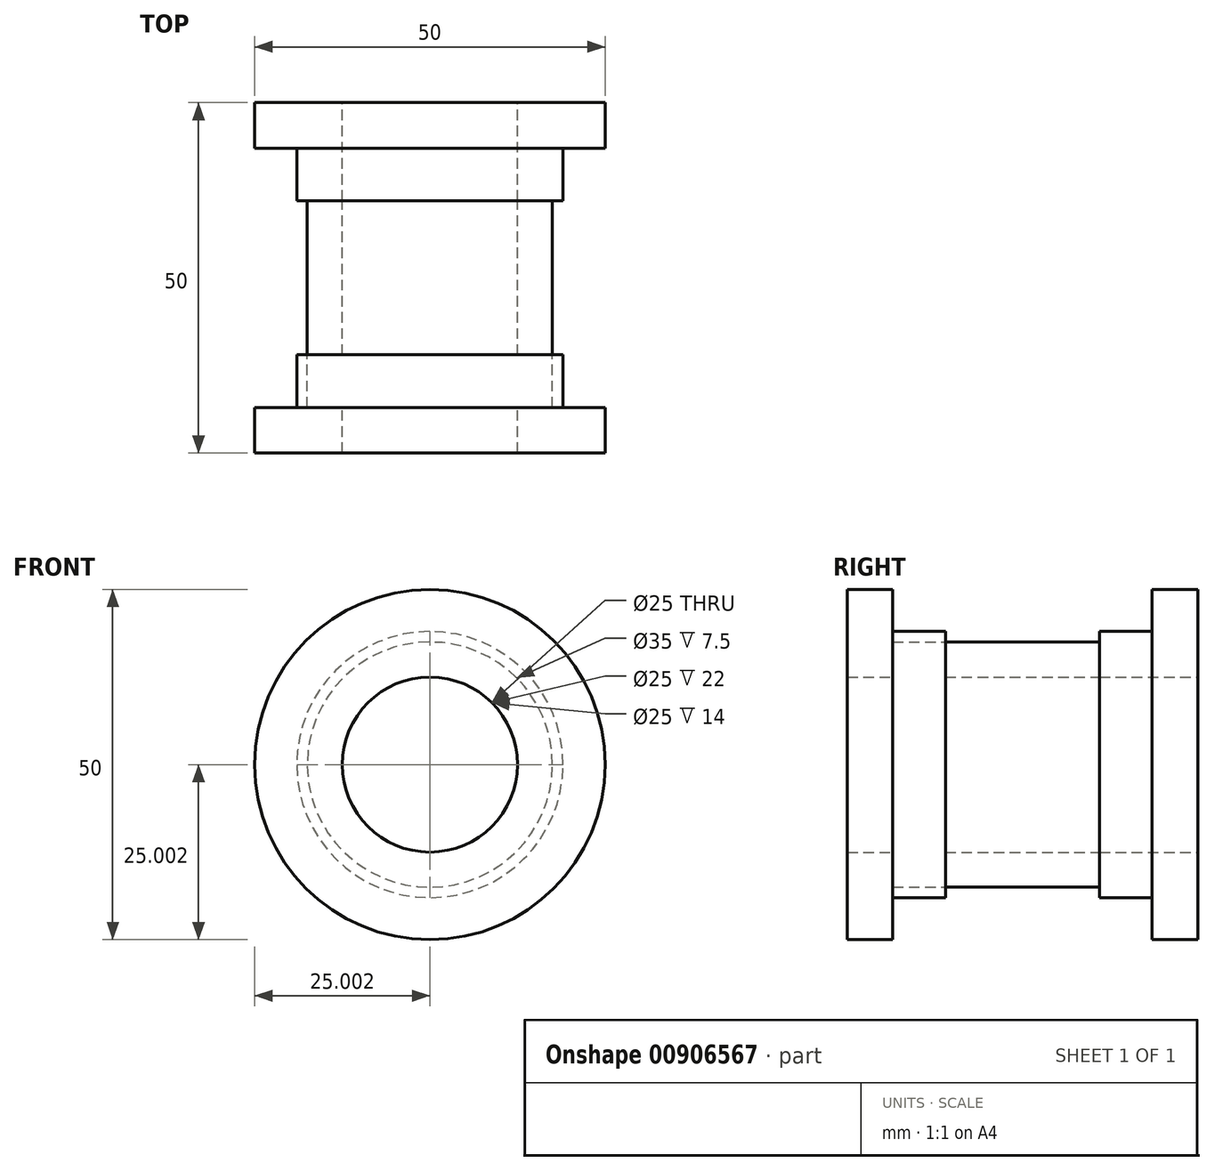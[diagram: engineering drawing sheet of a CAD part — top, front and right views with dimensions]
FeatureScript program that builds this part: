
annotation { "Feature Type Name" : "Feature", "Feature Type Description" : "" }
export const myFeature = defineFeature(function(context is Context, id is Id, definition is map)
    precondition{}
    {
        {
            var Q0;
            Q0=qCreatedBy(makeId("Front.planeOp"),FACE);
            var sketch = newSketch(context, id + "F0", { "sketchPlane" : qUnion([Q0])});
            skCircle(sketch, "E0", {"center": v(-103.9, 30.25) * mm, "radius": 25 * mm});
            skCircle(sketch, "E1", {"center": v(-103.9, 30.25) * mm, "radius": 12.5 * mm});
            skSolve(sketch);
        }
        {
            var Q0;
            Q0=makeQuery(id+"F0.imprint","IMPRINT",FACE,{"disambiguationData":[TD([[makeQuery(id+"F0.imprint","IMPRINT",EDGE,{"derivedFrom":sQuery(id+"F0.wireOp",EDGE,"E0")}),1.0]])]});
            extrude(context, id + "F1", {"entities" : qUnion([Q0]), "depth" : 6.5 * mm, "offsetDistance" : 25.4 * mm});
        }
        {
            var Q0;
            Q0=makeQuery(id+"F1.opExtrude","CAP_FACE",FACE,{"disambiguationData":[OSD([sQuery(id+"F0.wireOp",EDGE,"E0"),sQuery(id+"F0.wireOp",EDGE,"E1")])],"isStart":false});
            var sketch = newSketch(context, id + "F2", { "sketchPlane" : qUnion([Q0])});
            skCircle(sketch, "E2", {"center": v(-103.9, 30.25) * mm, "radius": 12.5 * mm});
            skCircle(sketch, "E3", {"center": v(-103.9, 30.25) * mm, "radius": 19 * mm});
            skSolve(sketch);
        }
        {
            var Q0;
            Q0=makeQuery(id+"F2.imprint","IMPRINT",FACE,{"disambiguationData":[TD([[makeQuery(id+"F2.imprint","IMPRINT",EDGE,{"derivedFrom":sQuery(id+"F2.wireOp",EDGE,"E2")}),-1.0]])]});
            extrude(context, id + "F3", {"entities" : qUnion([Q0]), "operationType" : NewBodyOperationType.ADD, "depth" : 7.5 * mm, "offsetDistance" : 25.4 * mm});
        }
        {
            var Q0;
            Q0=makeQuery(id+"F3.opExtrude","CAP_FACE",FACE,{"disambiguationData":[OSD([sQuery(id+"F2.wireOp",EDGE,"E2"),sQuery(id+"F2.wireOp",EDGE,"E3")])],"isStart":false});
            var sketch = newSketch(context, id + "F4", { "sketchPlane" : qUnion([Q0])});
            skCircle(sketch, "E4", {"center": v(-103.9, 30.25) * mm, "radius": 12.5 * mm});
            skCircle(sketch, "E5", {"center": v(-103.9, 30.25) * mm, "radius": 17.5 * mm});
            skSolve(sketch);
        }
        {
            var Q0;
            Q0=makeQuery(id+"F4.imprint","IMPRINT",FACE,{"disambiguationData":[TD([[makeQuery(id+"F4.imprint","IMPRINT",EDGE,{"derivedFrom":sQuery(id+"F4.wireOp",EDGE,"E4")}),-1.0]])]});
            extrude(context, id + "F5", {"entities" : qUnion([Q0]), "depth" : 22 * mm, "offsetDistance" : 25.4 * mm});
        }
        {
            var Q0;
            Q0=makeQuery(id+"F5.opExtrude","CAP_FACE",FACE,{"disambiguationData":[OSD([sQuery(id+"F4.wireOp",EDGE,"E4")])],"isStart":false});
            var sketch = newSketch(context, id + "F6", { "sketchPlane" : qUnion([Q0])});
            skCircle(sketch, "E6", {"center": v(-103.9, 30.25) * mm, "radius": 12.5 * mm});
            skCircle(sketch, "E7", {"center": v(-103.9, 30.25) * mm, "radius": 19 * mm});
            skSolve(sketch);
        }
        {
            var Q0;
            Q0=makeQuery(id+"F6.imprint","IMPRINT",FACE,{"disambiguationData":[TD([[makeQuery(id+"F6.imprint","IMPRINT",EDGE,{"derivedFrom":sQuery(id+"F6.wireOp",EDGE,"E7")}),1.0]])]});
            extrude(context, id + "F7", {"entities" : qUnion([Q0]), "depth" : 7.5 * mm, "offsetDistance" : 25.4 * mm});
        }
        {
            var Q0;
            Q0=makeQuery(id+"F7.opExtrude","CAP_FACE",FACE,{"disambiguationData":[OSD([sQuery(id+"F6.wireOp",EDGE,"E6"),sQuery(id+"F6.wireOp",EDGE,"E7")])],"isStart":false});
            var sketch = newSketch(context, id + "F8", { "sketchPlane" : qUnion([Q0])});
            skCircle(sketch, "E8", {"center": v(-103.9, 30.25) * mm, "radius": 12.5 * mm});
            skCircle(sketch, "E9", {"center": v(-103.9, 30.25) * mm, "radius": 25 * mm});
            skSolve(sketch);
        }
        {
            var Q0;
            Q0=makeQuery(id+"F8.imprint","IMPRINT",FACE,{"disambiguationData":[TD([[makeQuery(id+"F8.imprint","IMPRINT",EDGE,{"derivedFrom":sQuery(id+"F8.wireOp",EDGE,"E9")}),1.0]])]});
            var Q1;
            Q1=makeQuery(id+"F8.imprint","IMPRINT",FACE,{"disambiguationData":[TD([[makeQuery(id+"F8.imprint","IMPRINT",EDGE,{"derivedFrom":sQuery(id+"F8.wireOp",EDGE,"E8")}),-1.0]])]});
            var Q2;
            Q2=makeQuery(id+"F8.imprint","IMPRINT",FACE,{"disambiguationData":[TD([[makeQuery(id+"F8.imprint","IMPRINT",EDGE,{"derivedFrom":makeQuery(id+"F7.opExtrude","CAP_EDGE",EDGE,{"disambiguationData":[OSD([sQuery(id+"F6.wireOp",EDGE,"E7")])],"isStart":false})}),1.0]])]});
            extrude(context, id + "F9", {"entities" : qUnion([Q0, Q1, Q2]), "depth" : 6.5 * mm, "offsetDistance" : 25.4 * mm});
        }
    });
